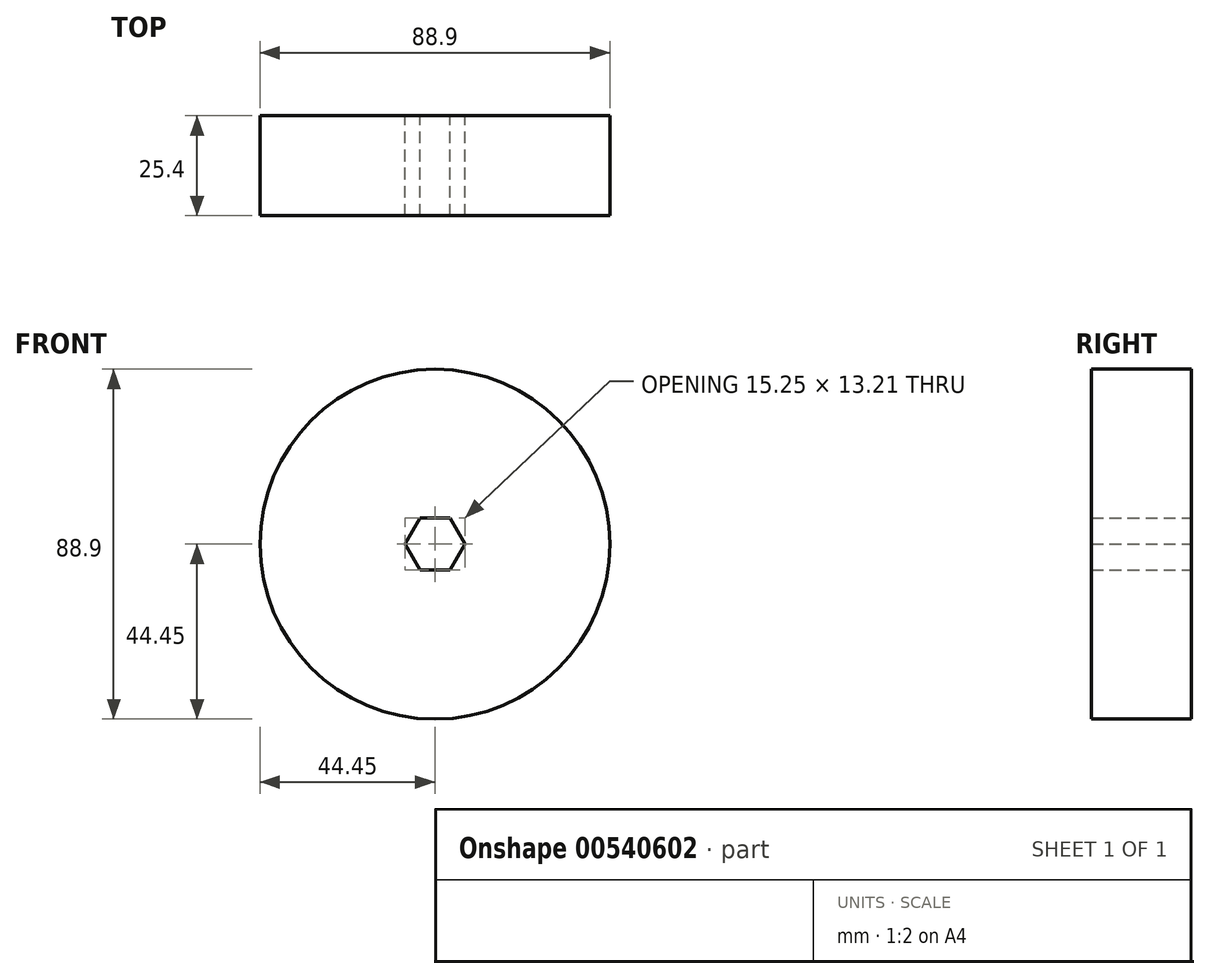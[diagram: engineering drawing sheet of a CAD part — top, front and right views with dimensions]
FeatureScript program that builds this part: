
annotation { "Feature Type Name" : "Feature", "Feature Type Description" : "" }
export const myFeature = defineFeature(function(context is Context, id is Id, definition is map)
    precondition{}
    {
        {
            var Q0;
            Q0=qCreatedBy(makeId("Front.planeOp"),FACE);
            var sketch = newSketch(context, id + "F0", { "sketchPlane" : qUnion([Q0])});
            skCircle(sketch, "E0.cCircle", {"center": v(0, 0) * mm, "radius": 6.6 * mm, "construction": true});
            skLineSegment(sketch, "E0.0", {"start": v(-3.81, 6.6) * mm, "end": v(3.81, 6.6) * mm});
            skLineSegment(sketch, "E0.1", {"start": v(3.81, 6.6) * mm, "end": v(7.63, 0) * mm});
            skLineSegment(sketch, "E0.2", {"start": v(7.63, 0) * mm, "end": v(3.81, -6.6) * mm});
            skLineSegment(sketch, "E0.3", {"start": v(3.81, -6.6) * mm, "end": v(-3.81, -6.6) * mm});
            skLineSegment(sketch, "E0.4", {"start": v(-3.81, -6.6) * mm, "end": v(-7.63, 0) * mm});
            skLineSegment(sketch, "E0.5", {"start": v(-7.63, 0) * mm, "end": v(-3.81, 6.6) * mm});
            skPoint(sketch, "E0.0.midPoint", {"position": v(0, 6.6) * mm});
            skCircle(sketch, "E1", {"center": v(0, 0) * mm, "radius": 44.45 * mm});
            skSolve(sketch);
        }
        {
            var Q0;
            Q0=makeQuery(id+"F0.imprint","IMPRINT",FACE,{"disambiguationData":[TD([[makeQuery(id+"F0.imprint","IMPRINT",EDGE,{"derivedFrom":sQuery(id+"F0.wireOp",EDGE,"E0.0")}),1.0]])]});
            extrude(context, id + "F1", {"entities" : qUnion([Q0]), "depth" : 25.4 * mm, "offsetDistance" : 25.4 * mm});
        }
    });
